# Revit family: Mark Tanner MDA verwarmer wandmontage
name_source: partatom
category: Mechanical Equipment
revit_build: Autodesk Revit 2017 (Build: 20160225_1515(x64)
units: mm (PartAtom-declared; Revit-internal decimal feet)

## family parameters
Always vertical = Yes
Cut with Voids When Loaded = No
OmniClass Number = 23.75.00.00
OmniClass Title = Climate Control (HVAC)
Part Type = Normal
Room Calculation Point = No
Round Connector Dimension = Use Diameter
Shared = No
Work Plane-Based = No

## types (42) — shared parameters
Manufacturer = Mark
URL = http://www.mark.nl

## per-type parameters (varying)
| type | Model | Type Comments | aantal_polen | artikelnummer | b1 | breedte | con 1_DN | con 1_RN | debiet | elektrisch_vermogen | gewicht | h1 | hoogte | l1 | l2 | lengte | nominale stroom | schijnbaar_vermogen | vermogen | voltage |
| Tanner MDA 121L | MDA 100 | MDA 121 ( 2 rijige wisselaar 1 fase 230 V fan waterzijdige aansluiting 1  laag toerental ) | 1 | MDA 121L | 380 mm | 380 mm | 25 mm | 13 mm | 5742.0 m³/h | 90 W | 22 | 450 mm  [stored 1.47638 ft] | 450 mm  [stored 1.47638 ft] | 450 mm  [stored 1.47638 ft] | 387 mm | 450 mm  [stored 1.47638 ft] | 0 A | 108 VA | 14500 W | 230 V |
| Tanner MDA 131L | MDA 100 | MDA 131 ( 3 rijige wisselaar  1 fase 230 V fan waterzijdige aansluiting 1 laag toerental) | 1 | MDA 131L | 380 mm | 380 mm | 25 mm | 13 mm | 5205.6 m³/h | 90 W | 23 | 450 mm  [stored 1.47638 ft] | 450 mm  [stored 1.47638 ft] | 450 mm  [stored 1.47638 ft] | 387 mm | 450 mm  [stored 1.47638 ft] | 0 A | 108 VA | 17000 W | 230 V |
| Tanner MDA 141L | MDA 100 | MDA 131 ( 4 rijige wisselaar  1 fase 230 V fan waterzijdige aansluiting 1 laag toerental) | 1 | MDA 141L | 380 mm | 380 mm | 25 mm | 13 mm | 4554.0 m³/h | 90 W | 24 | 450 mm  [stored 1.47638 ft] | 450 mm  [stored 1.47638 ft] | 450 mm  [stored 1.47638 ft] | 387 mm | 450 mm  [stored 1.47638 ft] | 0 A | 108 VA | 19000 W | 230 V |
| Tanner MDA 211L | MDA 200 | MDA 211 ( 1 rijige wisselaar  1 fase 230 V fanwaterzijdige aansluiting 1 laag toerental) | 1 | MDA 211L | 385 mm | 385 mm | 25 mm | 13 mm | 10098.0 m³/h | 120 W | 30 | 580 mm | 580 mm | 580 mm | 517 mm | 580 mm | 1 A | 117 VA | 14100 W | 230 V |
| Tanner MDA 221L | MDA 200 | MDA 221 ( 2 rijige wisselaar  1 fase 230 V fan waterzijdige aansluiting 1 laag toerental) | 1 | MDA 221L | 385 mm | 385 mm | 25 mm | 13 mm | 9561.6 m³/h | 120 W | 32 | 580 mm | 580 mm | 580 mm | 517 mm | 580 mm | 1 A | 117 VA | 25100 W | 230 V |
| Tanner MDA 231L | MDA 200 | MDA 231 ( 3 rijige wisselaar  1 fase 230 V fan waterzijdige aansluiting 1 laag toerental) | 1 | MDA 231L | 385 mm | 385 mm | 25 mm | 13 mm | 8571.6 m³/h | 120 W | 34 | 580 mm | 580 mm | 580 mm | 517 mm | 580 mm | 1 A | 117 VA | 30800 W | 230 V |
| Tanner MDA 241L | MDA 200 | MDA 241 ( 4 rijige wisselaar  1 fase 230 V fan waterzijdige aansluiting 1 laag toerental) | 1 | MDA 241L | 385 mm | 385 mm | 25 mm | 13 mm | 8028.0 m³/h | 120 W | 36 | 580 mm | 580 mm | 580 mm | 517 mm | 580 mm | 1 A | 117 VA | 33300 W | 230 V |
| Tanner MDA 321L | MDA 300 | MDA 321 ( 2 rijige wisselaar  1 fase 230 V fan waterzijdige aansluiting 1 laag toerental) | 1 | MDA 321L | 385 mm | 385 mm | 25 mm | 13 mm | 23382.0 m³/h | 330 W | 43 | 730 mm | 730 mm | 730 mm | 667 mm | 730 mm | 2 A | 391 VA | 52700 W | 230 V |
| Tanner MDA 331L | MDA 300 | MDA 331 ( 3 rijige wisselaar  1 fase 230 V fan waterzijdige aansluiting 11/4 laag toerental) | 1 | MDA 331L | 385 mm | 385 mm | 32 mm | 16 mm | 21085.2 m³/h | 330 W | 46 | 730 mm | 730 mm | 730 mm | 667 mm | 730 mm | 2 A | 391 VA | 65900 W | 230 V |
| Tanner MDA 341L | MDA 300 | MDA 341 ( 4 rijige wisselaar  1 fase 230 V fan waterzijdige aansluiting 11/4 laag toerental) | 1 | MDA 341L | 385 mm | 385 mm | 32 mm | 16 mm | 19522.8 m³/h | 330 W | 49 | 730 mm | 730 mm | 730 mm | 667 mm | 730 mm | 2 A | 391 VA | 72100 W | 230 V |
| Tanner MDA 411L | MDA 400 | MDA 411 ( 1 rijige wisselaar  1 fase 230 V fanwaterzijdige aansluiting 11/4 laag toerental) | 1 | MDA 411L | 405 mm | 405 mm | 32 mm | 16 mm | 37152.0 m³/h | 550 W | 51 | 860 mm | 860 mm | 860 mm | 667 mm | 860 mm | 3 A | 598 VA | 42500 W | 230 V |
| Tanner MDA 421L | MDA 400 | MDA 421 ( 2 rijige wisselaar  1 fase 230 V fanwaterzijdige aansluiting 11/4 laag toerental) | 1 | MDA 421L | 405 mm | 405 mm | 32 mm | 16 mm | 35758.8 m³/h | 550 W | 55 | 860 mm | 860 mm | 860 mm | 667 mm | 860 mm | 3 A | 598 VA | 80000 W | 230 V |
| Tanner MDA 431L | MDA 400 | MDA 431 ( 3 rijige wisselaar  1 fase 230 V fanwaterzijdige aansluiting 11/2 laag toerental) | 1 | MDA 431L | 405 mm | 405 mm | 40 mm | 20 mm | 31737.6 m³/h | 550 W | 59 | 860 mm | 860 mm | 860 mm | 667 mm | 860 mm | 3 A | 598 VA | 101000 W | 230 V |
| Tanner MDA 441L | MDA 400 | MDA 441 ( 4 rijige wisselaar  1 fase 230 V fanwaterzijdige aansluiting 11/2 laag toerental) | 1 | MDA 441L | 405 mm | 405 mm | 40 mm | 20 mm | 29581.2 m³/h | 550 W | 63 | 860 mm | 860 mm | 860 mm | 667 mm | 860 mm | 3 A | 598 VA | 110000 W | 230 V |
| Tanner MDA 121H | MDA 100 | MDA 121 ( 2 rijige wisselaar  1 fase 230 V fan waterzijdige aansluiting 1 hoog toerental) | 1 | MDA 121H | 380 mm | 380 mm | 25 mm | 13 mm | 8514.0 m³/h | 150 W | 22 | 450 mm  [stored 1.47638 ft] | 450 mm  [stored 1.47638 ft] | 450 mm  [stored 1.47638 ft] | 387 mm | 450 mm  [stored 1.47638 ft] | 1 A | 154 VA | 18000 W | 230 V |
| Tanner MDA 131H | MDA 100 | MDA 131 ( 3 rijige wisselaar  1 fase 230 V fan waterzijdige aansluiting 1 hoog toerental) | 1 | MDA 131H | 380 mm | 380 mm | 25 mm | 13 mm | 8078.4 m³/h | 150 W | 23 | 450 mm  [stored 1.47638 ft] | 450 mm  [stored 1.47638 ft] | 450 mm  [stored 1.47638 ft] | 387 mm | 450 mm  [stored 1.47638 ft] | 1 A | 154 VA | 22100 W | 230 V |
| Tanner MDA 141H | MDA 100 | MDA 131 ( 4 rijige wisselaar  1 fase 230 V fan waterzijdige aansluiting 1 hoog toerental) | 1 | MDA 141H | 380 mm | 380 mm | 25 mm | 13 mm | 6890.4 m³/h | 150 W | 24 | 450 mm  [stored 1.47638 ft] | 450 mm  [stored 1.47638 ft] | 450 mm  [stored 1.47638 ft] | 387 mm | 450 mm  [stored 1.47638 ft] | 1 A | 154 VA | 25100 W | 230 V |
| Tanner MDA 211H | MDA 200 | MDA 211 ( 1 rijige wisselaar  1 fase 230 V fan waterzijdige aansluiting 1 hoog toerental) | 1 | MDA 211H | 385 mm | 385 mm | 25 mm | 13 mm | 16020.0 m³/h | 280 W | 30 | 580 mm | 580 mm | 580 mm | 517 mm | 580 mm | 1 A | 311 VA | 17200 W | 230 V |
| Tanner MDA 221H | MDA 200 | MDA 221 ( 2 rijige wisselaar  1 fase 230 V fan waterzijdige aansluiting 1 hoog toerental) | 1 | MDA 221H | 385 mm | 385 mm | 25 mm | 13 mm | 15127.2 m³/h | 280 W | 32 | 580 mm | 580 mm | 580 mm | 517 mm | 580 mm | 1 A | 311 VA | 32400 W | 230 V |
| Tanner MDA 231H | MDA 200 | MDA 231 ( 3 rijige wisselaar  1 fase 230 V fan waterzijdige aansluiting 1 hoog toerental) | 1 | MDA 231H | 385 mm | 385 mm | 25 mm | 13 mm | 14155.2 m³/h | 280 W | 34 | 580 mm | 580 mm | 580 mm | 517 mm | 580 mm | 1 A | 311 VA | 42000 W | 230 V |
| Tanner MDA 241H | MDA 200 | MDA 241 ( 4 rijige wisselaar  1 fase 230 V fan waterzijdige aansluiting 1 hoog toerental) | 1 | MDA 241H | 385 mm | 385 mm | 25 mm | 13 mm | 13442.4 m³/h | 280 W | 34 | 580 mm | 580 mm | 580 mm | 517 mm | 580 mm | 1 A | 311 VA | 46600 W | 230 V |
| Tanner MDA 123L | MDA 100 | MDA 123 ( 2 rijige wisselaar  3 fase 400 V fan waterzijdige aansluiting 1 laag toerental) | 3 | MDA 123L | 380 mm | 380 mm | 25 mm | 13 mm | 5742.0 m³/h | 50 W | 22 | 450 mm  [stored 1.47638 ft] | 450 mm  [stored 1.47638 ft] | 450 mm  [stored 1.47638 ft] | 387 mm | 450 mm  [stored 1.47638 ft] | 0 A | 40 VA | 14500 W | 400 V |
| Tanner MDA 133L | MDA 100 | MDA 133 ( 3 rijige wisselaar  3 fase 400 V fan waterzijdige aansluiting 1 laag toerental) | 3 | MDA 133L | 380 mm | 380 mm | 25 mm | 13 mm | 5205.6 m³/h | 50 W | 23 | 450 mm  [stored 1.47638 ft] | 450 mm  [stored 1.47638 ft] | 450 mm  [stored 1.47638 ft] | 387 mm | 450 mm  [stored 1.47638 ft] | 0 A | 40 VA | 17000 W | 400 V |
| Tanner MDA 143L | MDA 100 | MDA 133 ( 4 rijige wisselaar  3 fase 400 V fan waterzijdige aansluiting 1 laag toerental) | 3 | MDA 143L | 380 mm | 380 mm | 25 mm | 13 mm | 4554.0 m³/h | 50 W | 24 | 450 mm  [stored 1.47638 ft] | 450 mm  [stored 1.47638 ft] | 450 mm  [stored 1.47638 ft] | 387 mm | 450 mm  [stored 1.47638 ft] | 0 A | 40 VA | 19000 W | 400 V |
| Tanner MDA 213L | MDA 200 | MDA 213 ( 1 rijige wisselaar  3 fase 400 V fan waterzijdige aansluiting 1 laag toerental) | 3 | MDA 213L | 385 mm | 385 mm | 25 mm | 13 mm | 10980.0 m³/h | 120 W | 30 | 580 mm | 580 mm | 580 mm | 517 mm | 580 mm | 0 A | 120 VA | 14800 W | 400 V |
| Tanner MDA 223L | MDA 200 | MDA 223 ( 2 rijige wisselaar  3 fase 400 V fan waterzijdige aansluiting 1 laag toerental) | 3 | MDA 223L | 385 mm | 385 mm | 25 mm | 13 mm | 10314.0 m³/h | 120 W | 32 | 580 mm | 580 mm | 580 mm | 517 mm | 580 mm | 0 A | 120 VA | 26200 W | 400 V |
| Tanner MDA 233L | MDA 200 | MDA 233 ( 3 rijige wisselaar  3 fase 400 V fan waterzijdige aansluiting 1 laag toerental) | 3 | MDA 233L | 385 mm | 385 mm | 25 mm | 13 mm | 9266.4 m³/h | 120 W | 34 | 580 mm | 580 mm | 580 mm | 517 mm | 580 mm | 0 A | 120 VA | 32400 W | 400 V |
| Tanner MDA 243L | MDA 200 | MDA 243 ( 4 rijige wisselaar  3 fase 400 V fan waterzijdige aansluiting 1 laag toerental) | 3 | MDA 243L | 385 mm | 385 mm | 25 mm | 13 mm | 8690.4 m³/h | 120 W | 36 | 580 mm | 580 mm | 580 mm | 517 mm | 580 mm | 0 A | 120 VA | 35100 W | 400 V |
| Tanner MDA 323L | MDA 300 | MDA 323 ( 2 rijige wisselaar  3 fase 400 V fan  waterzijdige aansluiting 1 laag toerental) | 3 | MDA 323L | 385 mm | 385 mm | 25 mm | 13 mm | 23382.0 m³/h | 280 W | 43 | 730 mm | 730 mm | 730 mm | 667 mm | 730 mm | 1 A | 272 VA | 52700 W | 400 V |
| Tanner MDA 333L | MDA 300 | MDA 333 ( 3 rijige wisselaar  3 fase 400 V fan  waterzijdige aansluiting 11/4 laag toerental) | 3 | MDA 333L | 385 mm | 385 mm | 32 mm | 16 mm | 21085.2 m³/h | 280 W | 46 | 730 mm | 730 mm | 730 mm | 667 mm | 730 mm | 1 A | 272 VA | 65900 W | 400 V |
| Tanner MDA 343L | MDA 300 | MDA 343 ( 4 rijige wisselaar  3 fase 400 V fan  waterzijdige aansluiting 11/4 laag toerental) | 3 | MDA 343L | 385 mm | 385 mm | 32 mm | 16 mm | 19522.8 m³/h | 280 W | 46 | 730 mm | 730 mm | 730 mm | 667 mm | 730 mm | 1 A | 272 VA | 72100 W | 400 V |
| Tanner MDA 413L | MDA 400 | MDA 413 ( 1 rijige wisselaar  3 fase 400 V fan  waterzijdige aansluiting 11/4 laag toerental) | 3 | MDA 413L | 405 mm | 405 mm | 32 mm | 16 mm | 41760.0 m³/h | 510 W | 52 | 860 mm | 860 mm | 860 mm | 667 mm | 860 mm | 2 A | 620 VA | 45200 W | 400 V |
| Tanner MDA 423L | MDA 400 | MDA 423 ( 2 rijige wisselaar  3 fase 400 V fan  waterzijdige aansluiting 11/4 laag toerental) | 3 | MDA 423L | 405 mm | 405 mm | 32 mm | 16 mm | 39124.8 m³/h | 510 W | 52 | 860 mm | 860 mm | 860 mm | 667 mm | 860 mm | 1 A | 400 VA | 84000 W | 400 V |
| Tanner MDA 433L | MDA 400 | MDA 433 ( 3 rijige wisselaar  3 fase 400 V fan  waterzijdige aansluiting 11/2 laag toerental) | 3 | MDA 433L | 405 mm | 405 mm | 40 mm | 20 mm | 35046.0 m³/h | 510 W | 61 | 860 mm | 860 mm | 860 mm | 667 mm | 860 mm | 1 A | 400 VA | 107000 W | 400 V |
| Tanner MDA 443L | MDA 400 | MDA 443 ( 4 rijige wisselaar  3 fase 400 V fan  waterzijdige aansluiting 11/2 laag toerental) | 3 | MDA 443L | 405 mm | 405 mm | 40 mm | 20 mm | 32630.4 m³/h | 510 W | 64 | 860 mm | 860 mm | 860 mm | 667 mm | 860 mm | 1 A | 400 VA | 117000 W | 400 V |
| Tanner MDA 123H | MDA 100 | MDA 123 ( 2 rijige wisselaar  3 fase 400 V fan waterzijdige aansluiting 1 hoog toerental) | 1 | MDA 123H | 380 mm | 380 mm | 25 mm | 13 mm | 8514.0 m³/h | 150 W | 22 | 450 mm  [stored 1.47638 ft] | 450 mm  [stored 1.47638 ft] | 450 mm  [stored 1.47638 ft] | 387 mm | 450 mm  [stored 1.47638 ft] | 0 A | 58 VA | 18000 W | 230 V |
| Tanner MDA 133H | MDA 100 | MDA 133 ( 3 rijige wisselaar  3 fase 400 V fan waterzijdige aansluiting 1 hoog toerental) | 1 | MDA 133H | 380 mm | 380 mm | 25 mm | 13 mm | 8078.4 m³/h | 150 W | 23 | 450 mm  [stored 1.47638 ft] | 450 mm  [stored 1.47638 ft] | 450 mm  [stored 1.47638 ft] | 387 mm | 450 mm  [stored 1.47638 ft] | 0 A | 58 VA | 22100 W | 230 V |
| Tanner MDA 143H | MDA 100 | MDA 133 ( 4 rijige wisselaar  3 fase 400 V fan waterzijdige aansluiting 1 hoog toerental) | 1 | MDA 143H | 380 mm | 380 mm | 25 mm | 13 mm | 6890.4 m³/h | 150 W | 24 | 450 mm  [stored 1.47638 ft] | 450 mm  [stored 1.47638 ft] | 450 mm  [stored 1.47638 ft] | 387 mm | 450 mm  [stored 1.47638 ft] | 0 A | 58 VA | 25100 W | 230 V |
| Tanner MDA 213H | MDA 200 | MDA 213 ( 1 rijige wisselaar  3 fase 400 V fan waterzijdige aansluiting 1 hoog toerental) | 1 | MDA 213H | 385 mm | 385 mm | 25 mm | 13 mm | 16020.0 m³/h | 280 W | 30 | 580 mm | 580 mm | 580 mm | 517 mm | 580 mm | 1 A | 154 VA | 17200 W | 230 V |
| Tanner MDA 223H | MDA 200 | MDA 223 ( 2 rijige wisselaar  3 fase 400 V fan waterzijdige aansluiting 1 hoog toerental) | 1 | MDA 223H | 385 mm | 385 mm | 25 mm | 13 mm | 15127.2 m³/h | 280 W | 32 | 580 mm | 580 mm | 580 mm | 517 mm | 580 mm | 1 A | 154 VA | 32400 W | 230 V |
| Tanner MDA 233H | MDA 200 | MDA 233 ( 3 rijige wisselaar  3 fase 400 V fan waterzijdige aansluiting 1 hoog toerental) | 1 | MDA 233H | 385 mm | 385 mm | 25 mm | 13 mm | 14155.2 m³/h | 280 W | 34 | 580 mm | 580 mm | 580 mm | 517 mm | 580 mm | 1 A | 154 VA | 42000 W | 230 V |
| Tanner MDA 243H | MDA 200 | MDA 243 ( 4 rijige wisselaar  3 fase 400 V fan waterzijdige aansluiting 1 hoog toerental) | 1 | MDA 243H | 385 mm | 385 mm | 25 mm | 13 mm | 13442.4 m³/h | 280 W | 34 | 580 mm | 580 mm | 580 mm | 517 mm | 580 mm | 1 A | 154 VA | 46600 W | 230 V |

note: [stored X ft] marks values corroborated as IEEE doubles in the binary element streams (Revit-internal decimal feet)

## geometry (parser evidence)
native form markers: Sweep x10
no freeform markers — native parametric forms only
